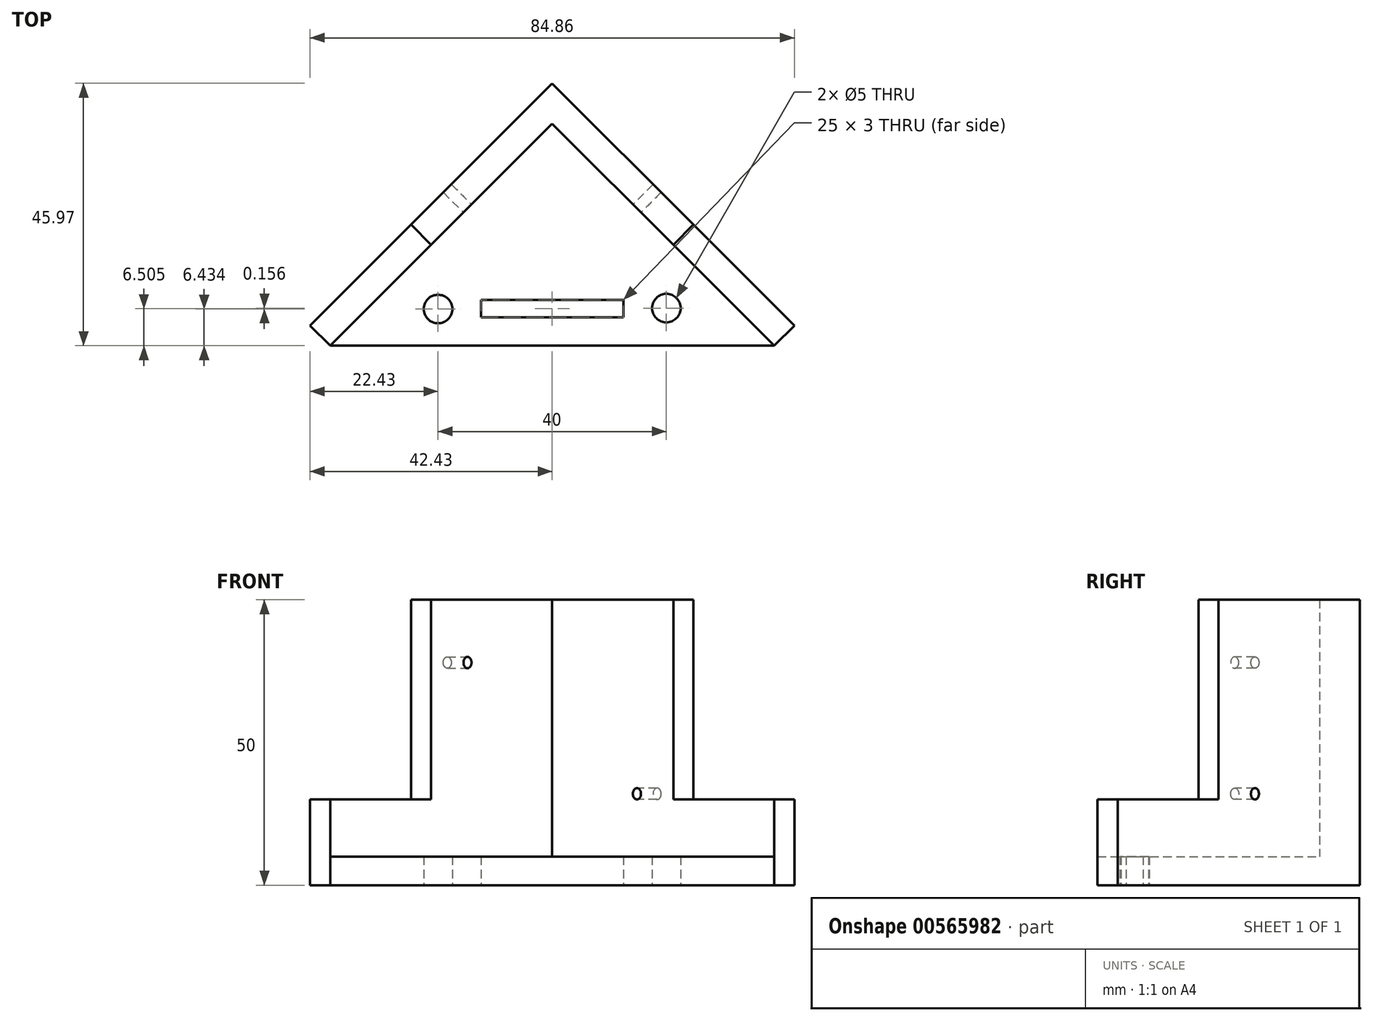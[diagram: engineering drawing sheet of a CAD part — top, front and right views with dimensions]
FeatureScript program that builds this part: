
annotation { "Feature Type Name" : "Feature", "Feature Type Description" : "" }
export const myFeature = defineFeature(function(context is Context, id is Id, definition is map)
    precondition{}
    {
        {
            var Q0;
            Q0=qCreatedBy(makeId("Top.planeOp"),FACE);
            var sketch = newSketch(context, id + "F0", { "sketchPlane" : qUnion([Q0])});
            skPoint(sketch, "E0", {"position": v(0, 42.43) * mm});
            skPoint(sketch, "E1", {"position": v(-42.43, 0) * mm});
            skPoint(sketch, "E2", {"position": v(42.43, 0) * mm});
            skLineSegment(sketch, "E3", {"start": v(-42.43, 0) * mm, "end": v(0, 42.43) * mm});
            skLineSegment(sketch, "E4", {"start": v(42.43, 0) * mm, "end": v(0, 42.43) * mm});
            skLineSegment(sketch, "E5", {"start": v(-42.43, 0) * mm, "end": v(-38.9, -3.54) * mm});
            skLineSegment(sketch, "E6", {"start": v(-38.9, -3.54) * mm, "end": v(0, 35.36) * mm});
            skLineSegment(sketch, "E7", {"start": v(0, 35.36) * mm, "end": v(38.9, -3.54) * mm});
            skLineSegment(sketch, "E8", {"start": v(38.9, -3.54) * mm, "end": v(42.43, 0) * mm});
            skSolve(sketch);
        }
        {
            var Q0;
            Q0=makeQuery(id+"F0.imprint","IMPRINT",FACE,{"disambiguationData":[TD([[makeQuery(id+"F0.imprint","IMPRINT",EDGE,{"derivedFrom":sQuery(id+"F0.wireOp",EDGE,"E3")}),-1.0]])]});
            var Q1;
            {var subQ3=sQuery(id+"F0.wireOp",EDGE,"Ov8XaEAz-VJQk-u9B9-b4jE-GfAUFlwIgoER");Q1=makeQuery(id+"F0.imprint","IMPRINT",FACE,{"disambiguationData":[TD([[makeQuery(id+"F0.imprint","IMPRINT",EDGE,{"derivedFrom":subQ3}),1.0]])]});}
            extrude(context, id + "F1", {"entities" : qUnion([Q0, Q1]), "depth" : 50 * mm, "offsetDistance" : 25 * mm});
        }
        {
            var Q0;
            Q0=makeQuery(id+"F1.opExtrude","CAP_FACE",FACE,{"disambiguationData":[OSD([sQuery(id+"F0.wireOp",EDGE,"E3"),sQuery(id+"F0.wireOp",EDGE,"E4"),sQuery(id+"F0.wireOp",EDGE,"E5"),sQuery(id+"F0.wireOp",EDGE,"E6"),sQuery(id+"F0.wireOp",EDGE,"E7"),sQuery(id+"F0.wireOp",EDGE,"E8")])],"isStart":true});
            var sketch = newSketch(context, id + "F2", { "sketchPlane" : qUnion([Q0])});
            skLineSegment(sketch, "E9", {"start": v(-38.9, 3.54) * mm, "end": v(38.9, 3.54) * mm});
            skSolve(sketch);
        }
        {
            var Q0;
            Q0=makeQuery(id+"F2.imprint","IMPRINT",FACE,{"disambiguationData":[TD([[makeQuery(id+"F2.imprint","IMPRINT",EDGE,{"derivedFrom":sQuery(id+"F2.wireOp",EDGE,"E9")}),-1.0]])]});
            extrude(context, id + "F3", {"entities" : qUnion([Q0]), "operationType" : NewBodyOperationType.ADD, "oppositeDirection" : true, "depth" : 5 * mm, "offsetDistance" : 25 * mm});
        }
        {
            var Q0;
            {var subQ0=sQuery(id+"F0.wireOp",EDGE,"E7");var subQ1=sQuery(id+"F0.wireOp",EDGE,"E6");Q0=makeQuery(id+"F3.boolean.opBoolean","MERGE",FACE,{"derivedFrom":[makeQuery(id+"F1.opExtrude","CAP_FACE",FACE,{"disambiguationData":[OSD([sQuery(id+"F0.wireOp",EDGE,"E3"),sQuery(id+"F0.wireOp",EDGE,"E4"),sQuery(id+"F0.wireOp",EDGE,"E5"),subQ1,subQ0,sQuery(id+"F0.wireOp",EDGE,"E8")])],"isStart":true}),makeQuery(id+"F3.opExtrude","CAP_FACE",FACE,{"disambiguationData":[OSD([subQ1,subQ0,sQuery(id+"F2.wireOp",EDGE,"E9")])],"isStart":true})]});}
            var sketch = newSketch(context, id + "F4", { "sketchPlane" : qUnion([Q0])});
            skLineSegment(sketch, "E10.bottom", {"start": v(-12.5, -1.46) * mm, "end": v(12.5, -1.46) * mm});
            skLineSegment(sketch, "E10.top", {"start": v(-12.5, -4.46) * mm, "end": v(12.5, -4.46) * mm});
            skLineSegment(sketch, "E10.left", {"start": v(-12.5, -1.46) * mm, "end": v(-12.5, -4.46) * mm});
            skLineSegment(sketch, "E10.right", {"start": v(12.5, -1.46) * mm, "end": v(12.5, -4.46) * mm});
            skPoint(sketch, "E10.middle", {"position": v(0, -2.96) * mm});
            skCircle(sketch, "E11", {"center": v(20, -3.05) * mm, "radius": 2.5 * mm});
            skCircle(sketch, "E12", {"center": v(-20, -2.9) * mm, "radius": 2.5 * mm});
            skSolve(sketch);
        }
        {
            var Q0;
            Q0=makeQuery(id+"F4.imprint","IMPRINT",FACE,{"disambiguationData":[TD([[makeQuery(id+"F4.imprint","IMPRINT",EDGE,{"derivedFrom":sQuery(id+"F4.wireOp",EDGE,"E10.bottom")}),-1.0]])]});
            var Q1;
            Q1=makeQuery(id+"F4.imprint","IMPRINT",FACE,{"disambiguationData":[TD([[makeQuery(id+"F4.imprint","IMPRINT",EDGE,{"derivedFrom":sQuery(id+"F4.wireOp",EDGE,"E11")}),1.0]])]});
            var Q2;
            Q2=makeQuery(id+"F4.imprint","IMPRINT",FACE,{"disambiguationData":[TD([[makeQuery(id+"F4.imprint","IMPRINT",EDGE,{"derivedFrom":sQuery(id+"F4.wireOp",EDGE,"E12")}),1.0]])]});
            extrude(context, id + "F5", {"entities" : qUnion([Q0, Q1, Q2]), "operationType" : NewBodyOperationType.REMOVE, "oppositeDirection" : true, "depth" : 25 * mm, "offsetDistance" : 25 * mm});
        }
        {
            var Q0;
            Q0=makeQuery(id+"F1.opExtrude","SWEPT_FACE",FACE,{"disambiguationData":[OSD([sQuery(id+"F0.wireOp",EDGE,"E6")])]});
            var sketch = newSketch(context, id + "F6", { "sketchPlane" : qUnion([Q0])});
            skCircle(sketch, "E13", {"center": v(4, 39) * mm, "radius": 1 * mm});
            skSolve(sketch);
        }
        {
            var Q0;
            Q0=makeQuery(id+"F1.opExtrude","SWEPT_FACE",FACE,{"disambiguationData":[OSD([sQuery(id+"F0.wireOp",EDGE,"E7")])]});
            var sketch = newSketch(context, id + "F7", { "sketchPlane" : qUnion([Q0])});
            skCircle(sketch, "E14", {"center": v(-4, 16) * mm, "radius": 1 * mm});
            skSolve(sketch);
        }
        {
            var Q0;
            Q0=makeQuery(id+"F6.imprint","IMPRINT",FACE,{"disambiguationData":[TD([[makeQuery(id+"F6.imprint","IMPRINT",EDGE,{"derivedFrom":sQuery(id+"F6.wireOp",EDGE,"E13")}),1.0]])]});
            extrude(context, id + "F8", {"entities" : qUnion([Q0]), "operationType" : NewBodyOperationType.REMOVE, "oppositeDirection" : true, "depth" : 25 * mm, "offsetDistance" : 25 * mm});
        }
        {
            var Q0;
            Q0=makeQuery(id+"F7.imprint","IMPRINT",FACE,{"disambiguationData":[TD([[makeQuery(id+"F7.imprint","IMPRINT",EDGE,{"derivedFrom":sQuery(id+"F7.wireOp",EDGE,"E14")}),1.0]])]});
            extrude(context, id + "F9", {"entities" : qUnion([Q0]), "operationType" : NewBodyOperationType.REMOVE, "oppositeDirection" : true, "depth" : 25 * mm, "offsetDistance" : 25 * mm});
        }
        {
            var Q0;
            Q0=makeQuery(id+"F1.opExtrude","SWEPT_FACE",FACE,{"disambiguationData":[OSD([sQuery(id+"F0.wireOp",EDGE,"E6")])]});
            var sketch = newSketch(context, id + "F10", { "sketchPlane" : qUnion([Q0])});
            skCircle(sketch, "E15", {"center": v(4, 39) * mm, "radius": 1.75 * mm});
            skSolve(sketch);
        }
        {
            var Q0;
            Q0=makeQuery(id+"F1.opExtrude","SWEPT_FACE",FACE,{"disambiguationData":[OSD([sQuery(id+"F0.wireOp",EDGE,"E7")])]});
            var sketch = newSketch(context, id + "F11", { "sketchPlane" : qUnion([Q0])});
            skCircle(sketch, "E16", {"center": v(-4, 16) * mm, "radius": 1.75 * mm});
            skSolve(sketch);
        }
        {
            var Q0;
            Q0=makeQuery(id+"F1.opExtrude","CAP_FACE",FACE,{"disambiguationData":[OSD([sQuery(id+"F0.wireOp",EDGE,"E3"),sQuery(id+"F0.wireOp",EDGE,"E4"),sQuery(id+"F0.wireOp",EDGE,"E5"),sQuery(id+"F0.wireOp",EDGE,"E6"),sQuery(id+"F0.wireOp",EDGE,"E7"),sQuery(id+"F0.wireOp",EDGE,"E8")])],"isStart":false});
            var sketch = newSketch(context, id + "F12", { "sketchPlane" : qUnion([Q0])});
            skLineSegment(sketch, "E17", {"start": v(-21.21, 14.14) * mm, "end": v(-24.75, 17.68) * mm});
            skLineSegment(sketch, "E18", {"start": v(21.21, 14.14) * mm, "end": v(24.75, 17.68) * mm});
            skSolve(sketch);
        }
        {
            var Q0;
            {var subQ0=sQuery(id+"F12.wireOp",EDGE,"E17");Q0=makeQuery(id+"F12.imprint","IMPRINT",FACE,{"disambiguationData":[TD([[makeQuery(id+"F12.imprint","IMPRINT",EDGE,{"derivedFrom":subQ0}),1.0]])]});}
            var Q1;
            {var subQ0=sQuery(id+"F12.wireOp",EDGE,"E18");Q1=makeQuery(id+"F12.imprint","IMPRINT",FACE,{"disambiguationData":[TD([[makeQuery(id+"F12.imprint","IMPRINT",EDGE,{"derivedFrom":subQ0}),-1.0]])]});}
            extrude(context, id + "F13", {"entities" : qUnion([Q0, Q1]), "operationType" : NewBodyOperationType.REMOVE, "oppositeDirection" : true, "depth" : 35 * mm, "offsetDistance" : 25 * mm});
        }
    });
